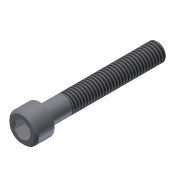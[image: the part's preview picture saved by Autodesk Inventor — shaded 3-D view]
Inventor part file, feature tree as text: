
AUTODESK INVENTOR PART (.ipt)
format: ipt  version: 2013 (Build 170138000, 138)  size: 124,416 bytes
history: native  units: in
note: dims shown in document units (in); Inventor stores cm internally (conversion verified against a paired STEP export)
features: extrude x4, sketch x4, chamfer x3, thread x1
ambient origin geometry x8: Origin, YZ Plane, XZ Plane, XY Plane, X Axis, Y Axis, Z Axis, Center Point
bodies: Solid1 (feature_tree)
feature tree (12):
  extrude  "Extrusion1"  TaperAngle=0.0deg  [1 undecoded]
  extrude  "Extrusion2"  Depth=0.125in TaperAngle=45.0deg
  thread  "Thread1"  [1 undecoded]
  chamfer  "Chamfer1"  Distance=0.012in
  chamfer  "Chamfer2"  Distance=0.012in Angle=45.0deg
  extrude  "Extrusion4"  Depth=0.117in TaperAngle=0.0deg
  chamfer  "Chamfer3"  [1 undecoded]
  extrude  "Extrusion5"  [1 undecoded]
  sketch  "Sketch1"  dims[d2=0.0in d5=0.0in]
  sketch  "Sketch2"  dims[d10=0.0in d12=0.125in d13=45.0deg d15=0.125in d16=45.0deg]
  sketch  "Sketch4"  dims[d21=0.1562in d22=0.012in d23=0.0in d24=0.012in d25=0.125in d26=45.0deg]
  sketch  "Sketch5"  dims[d27=0.1562in d28=0.117in d29=0.0in]
note: 4 required parameter values undecoded (feature->parameter linkage not recoverable at this tier; creation-order binding heuristic only, values carry confidence <= 0.55)
